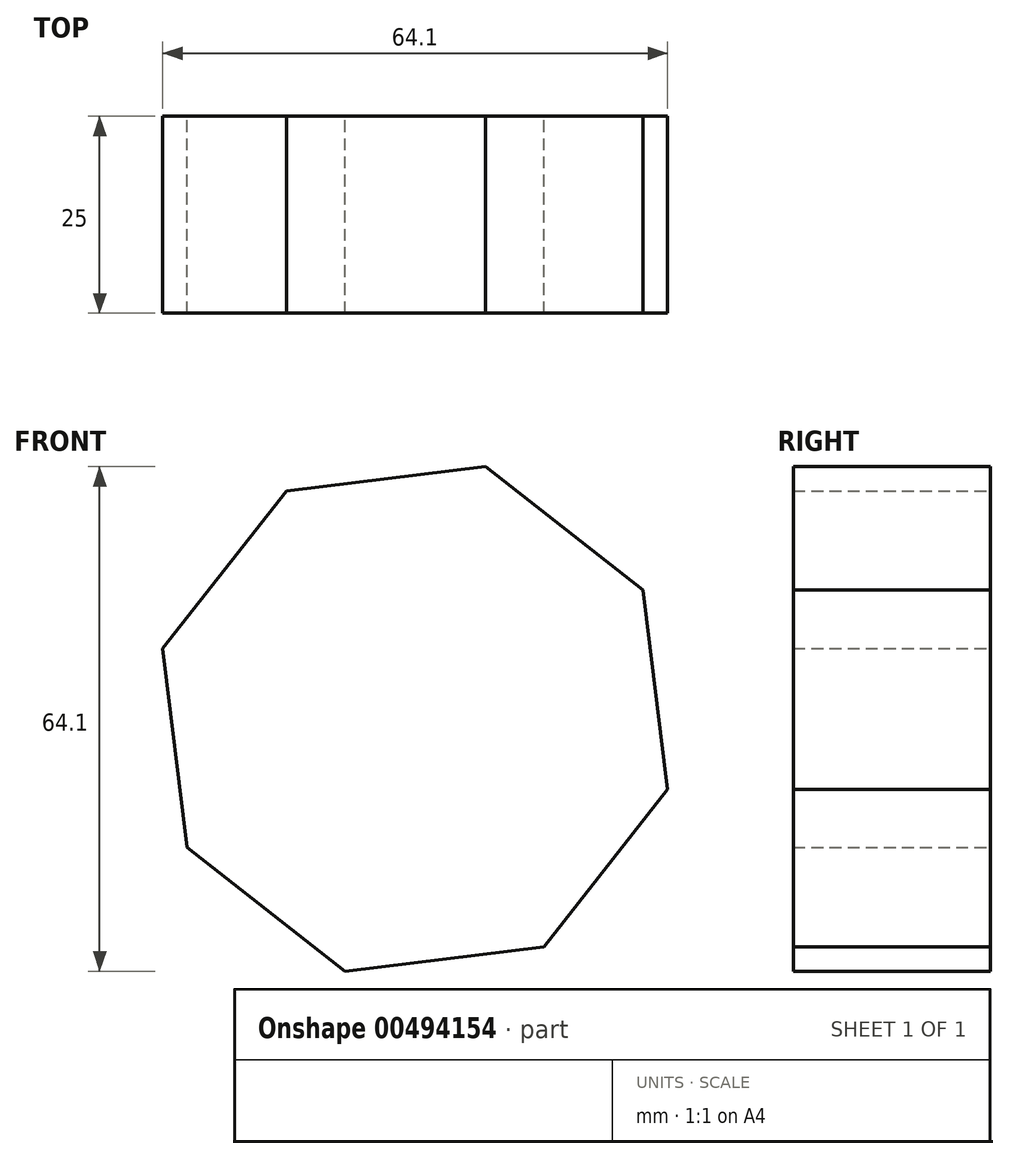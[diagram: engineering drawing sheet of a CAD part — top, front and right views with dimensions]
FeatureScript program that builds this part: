
annotation { "Feature Type Name" : "Feature", "Feature Type Description" : "" }
export const myFeature = defineFeature(function(context is Context, id is Id, definition is map)
    precondition{}
    {
        {
            var Q0;
            Q0=qCreatedBy(makeId("Front.planeOp"),FACE);
            var sketch = newSketch(context, id + "F0", { "sketchPlane" : qUnion([Q0])});
            skCircle(sketch, "E0.cCircle", {"center": v(-11.76, 15.35) * mm, "radius": 33.27 * mm, "construction": true});
            skLineSegment(sketch, "E0.0", {"start": v(4.6, -13.63) * mm, "end": v(-20.69, -16.7) * mm});
            skLineSegment(sketch, "E0.1", {"start": v(-20.69, -16.7) * mm, "end": v(-40.74, -1) * mm});
            skLineSegment(sketch, "E0.2", {"start": v(-40.74, -1) * mm, "end": v(-43.81, 24.27) * mm});
            skLineSegment(sketch, "E0.3", {"start": v(-43.81, 24.27) * mm, "end": v(-28.11, 44.32) * mm});
            skLineSegment(sketch, "E0.4", {"start": v(-28.11, 44.32) * mm, "end": v(-2.84, 47.4) * mm});
            skLineSegment(sketch, "E0.5", {"start": v(-2.84, 47.4) * mm, "end": v(17.21, 31.7) * mm});
            skLineSegment(sketch, "E0.6", {"start": v(17.21, 31.7) * mm, "end": v(20.29, 6.42) * mm});
            skLineSegment(sketch, "E0.7", {"start": v(20.29, 6.42) * mm, "end": v(4.6, -13.63) * mm});
            skSolve(sketch);
        }
        {
            var Q0;
            Q0=makeQuery(id+"F0.imprint","IMPRINT",FACE,{"disambiguationData":[TD([[makeQuery(id+"F0.imprint","IMPRINT",EDGE,{"derivedFrom":sQuery(id+"F0.wireOp",EDGE,"E0.0")}),-1.0]])]});
            extrude(context, id + "F1", {"entities" : qUnion([Q0]), "depth" : 25 * mm});
        }
    });
